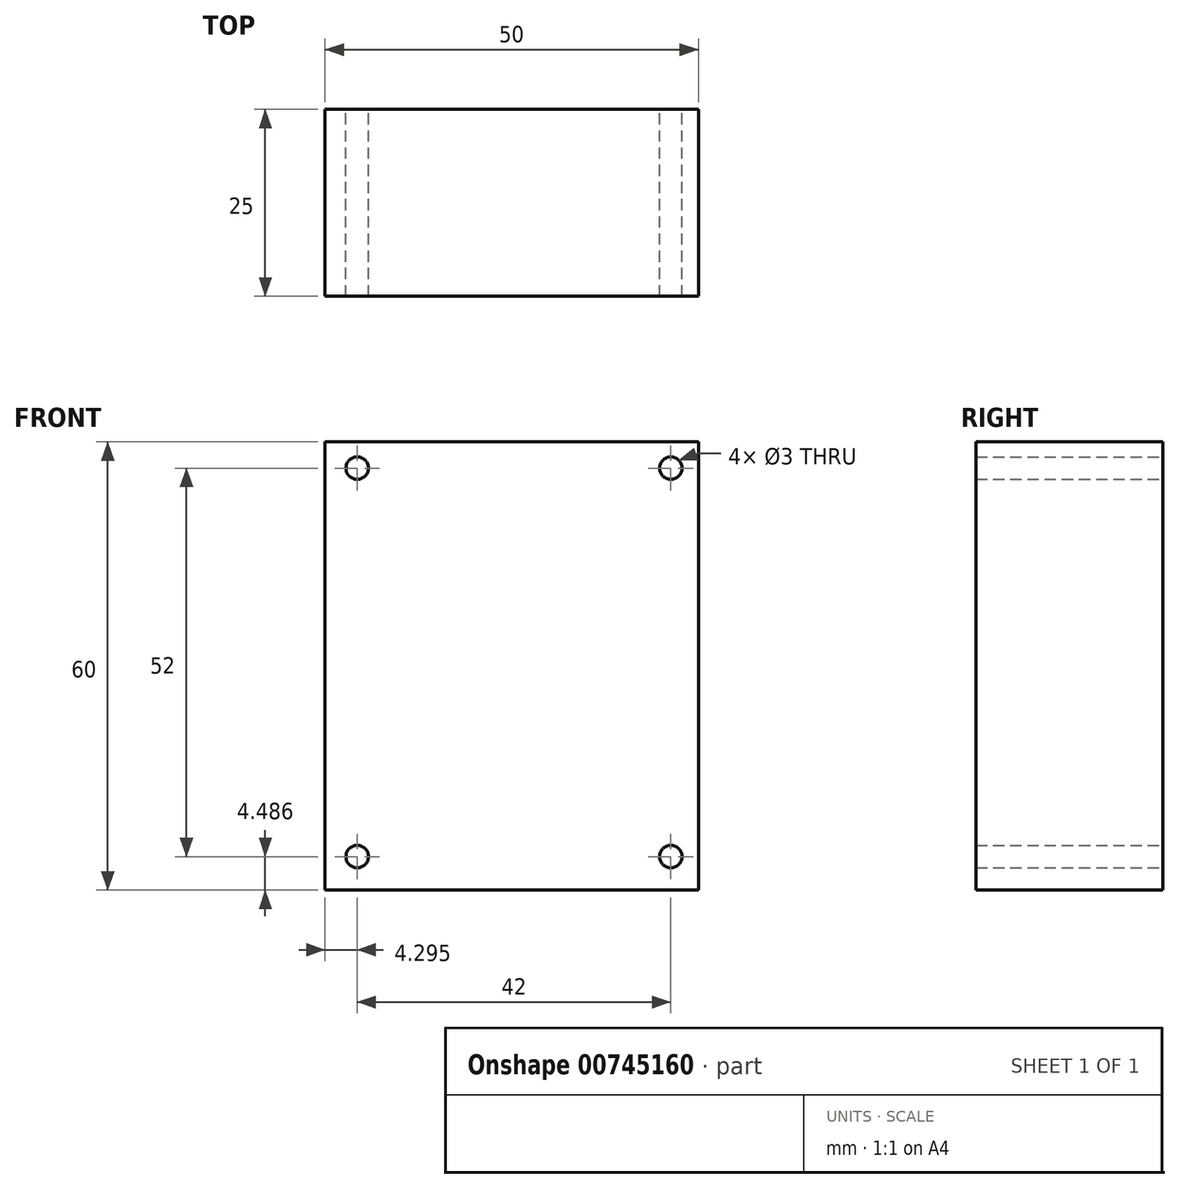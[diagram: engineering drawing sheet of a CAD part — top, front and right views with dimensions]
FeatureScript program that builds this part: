
annotation { "Feature Type Name" : "Feature", "Feature Type Description" : "" }
export const myFeature = defineFeature(function(context is Context, id is Id, definition is map)
    precondition{}
    {
        {
            var Q0;
            Q0=qCreatedBy(makeId("Front.planeOp"),FACE);
            var sketch = newSketch(context, id + "F0", { "sketchPlane" : qUnion([Q0])});
            skLineSegment(sketch, "E0.bottom", {"start": v(0, 0) * mm, "end": v(50, 0) * mm});
            skLineSegment(sketch, "E0.top", {"start": v(0, -60) * mm, "end": v(50, -60) * mm});
            skLineSegment(sketch, "E0.left", {"start": v(0, 0) * mm, "end": v(0, -60) * mm});
            skLineSegment(sketch, "E0.right", {"start": v(50, 0) * mm, "end": v(50, -60) * mm});
            skSolve(sketch);
        }
        {
            var Q0;
            Q0=makeQuery(id+"F0.imprint","IMPRINT",FACE,{"disambiguationData":[TD([[makeQuery(id+"F0.imprint","IMPRINT",EDGE,{"derivedFrom":sQuery(id+"F0.wireOp",EDGE,"E0.bottom")}),-1.0]])]});
            var sketch = newSketch(context, id + "F1", { "sketchPlane" : qUnion([Q0])});
            skCircle(sketch, "E1", {"center": v(4.3, -55.51) * mm, "radius": 1.5 * mm});
            skCircle(sketch, "E2", {"center": v(46.3, -55.51) * mm, "radius": 1.5 * mm});
            skCircle(sketch, "E3", {"center": v(4.3, -3.51) * mm, "radius": 1.5 * mm});
            skCircle(sketch, "E4", {"center": v(46.3, -3.51) * mm, "radius": 1.5 * mm});
            skSolve(sketch);
        }
        {
            var Q0;
            Q0=makeQuery(id+"F0.imprint","IMPRINT",FACE,{"disambiguationData":[TD([[makeQuery(id+"F0.imprint","IMPRINT",EDGE,{"derivedFrom":sQuery(id+"F0.wireOp",EDGE,"E0.bottom")}),-1.0]])]});
            var Q1;
            Q1=makeQuery(id+"F1.imprint","IMPRINT",FACE,{"disambiguationData":[TD([[makeQuery(id+"F1.imprint","IMPRINT",EDGE,{"derivedFrom":sQuery(id+"F1.wireOp",EDGE,"E1")}),-1.0]])]});
            extrude(context, id + "F2", {"entities" : qUnion([Q0, Q1]), "depth" : 25 * mm, "offsetDistance" : 25 * mm});
        }
    });
